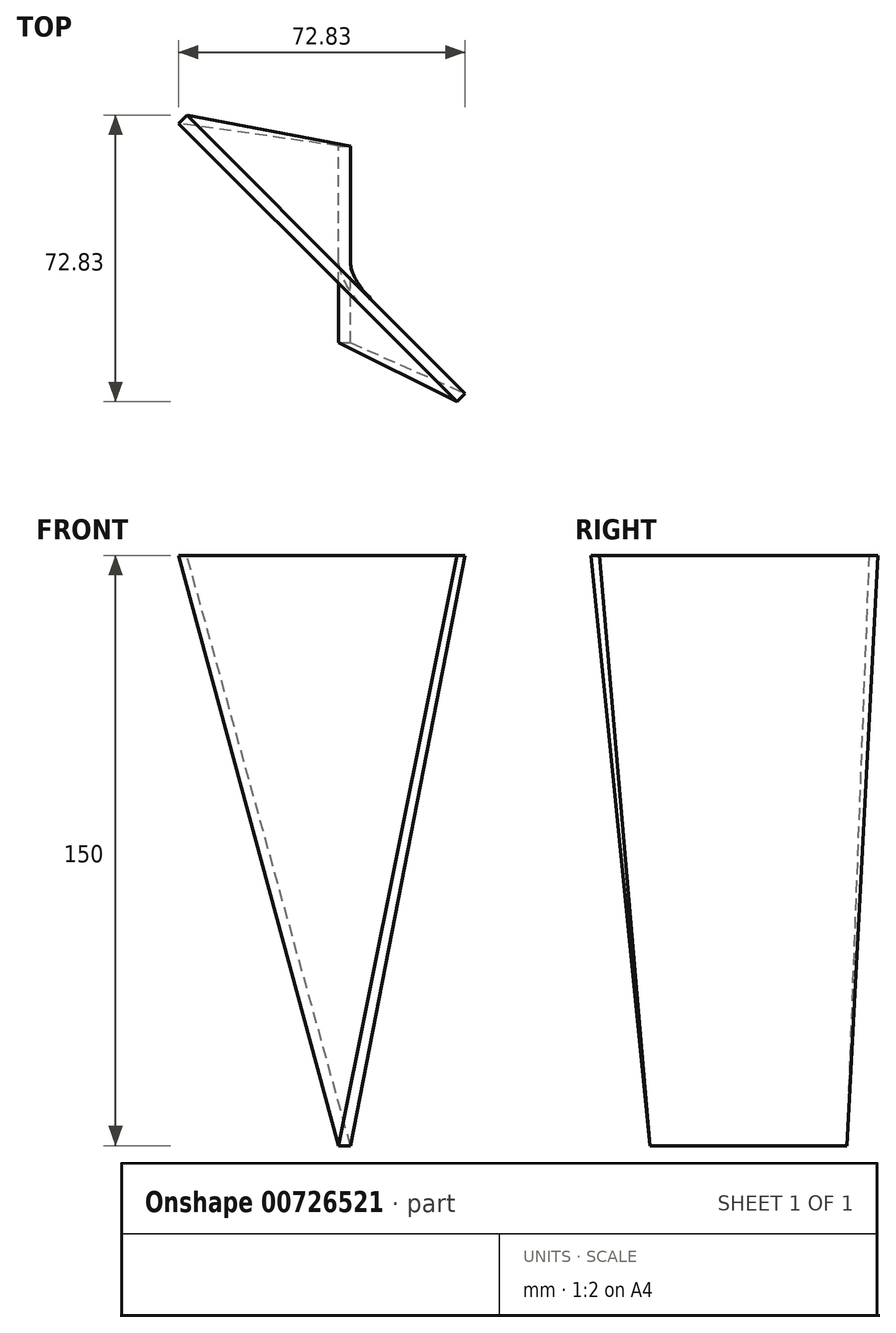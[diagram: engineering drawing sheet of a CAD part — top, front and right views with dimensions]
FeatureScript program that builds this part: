
annotation { "Feature Type Name" : "Feature", "Feature Type Description" : "" }
export const myFeature = defineFeature(function(context is Context, id is Id, definition is map)
    precondition{}
    {
        {
            var Q0;
            Q0=qCreatedBy(makeId("Top.planeOp"),FACE);
            var sketch = newSketch(context, id + "F0", { "sketchPlane" : qUnion([Q0])});
            skLineSegment(sketch, "E0.bottom", {"start": v(0, 0) * mm, "end": v(3, 0) * mm});
            skLineSegment(sketch, "E0.top", {"start": v(0, 50) * mm, "end": v(3, 50) * mm});
            skLineSegment(sketch, "E0.left", {"start": v(0, 0) * mm, "end": v(0, 50) * mm});
            skLineSegment(sketch, "E0.right", {"start": v(3, 0) * mm, "end": v(3, 50) * mm});
            skSolve(sketch);
        }
        {
            var Q0;
            Q0=qCreatedBy(makeId("Top.planeOp"),FACE);
            cPlane(context, id + "F1", {"entities" : qUnion([Q0]), "cplaneType" : CPlaneType.OFFSET, "offset" : 150 * mm, "width" : 150 * mm, "height" : 150 * mm});
        }
        {
            var Q0;
            Q0=qCreatedBy(id+"F1.planeOp",FACE);
            var sketch = newSketch(context, id + "F2", { "sketchPlane" : qUnion([Q0])});
            skLineSegment(sketch, "E1.bottom", {"start": v(30, -15) * mm, "end": v(32.12, -12.88) * mm});
            skLineSegment(sketch, "E1.top", {"start": v(-40.71, 55.71) * mm, "end": v(-38.59, 57.83) * mm});
            skLineSegment(sketch, "E1.left", {"start": v(30, -15) * mm, "end": v(-40.71, 55.71) * mm});
            skLineSegment(sketch, "E1.right", {"start": v(32.12, -12.88) * mm, "end": v(-38.59, 57.83) * mm});
            skSolve(sketch);
        }
        {
            var Q0;
            Q0=makeQuery(id+"F0.imprint","IMPRINT",FACE,{"disambiguationData":[TD([[makeQuery(id+"F0.imprint","IMPRINT",EDGE,{"derivedFrom":sQuery(id+"F0.wireOp",EDGE,"E0.bottom")}),1.0]])]});
            var Q1;
            Q1=makeQuery(id+"F2.imprint","IMPRINT",FACE,{"disambiguationData":[TD([[makeQuery(id+"F2.imprint","IMPRINT",EDGE,{"derivedFrom":sQuery(id+"F2.wireOp",EDGE,"E1.bottom")}),1.0]])]});
            loft(context, id + "F3", {"sheetProfilesArray" : [{ "sheetProfileEntities" : qUnion([Q0]) }, { "sheetProfileEntities" : qUnion([Q1]) }]});
        }
    });
